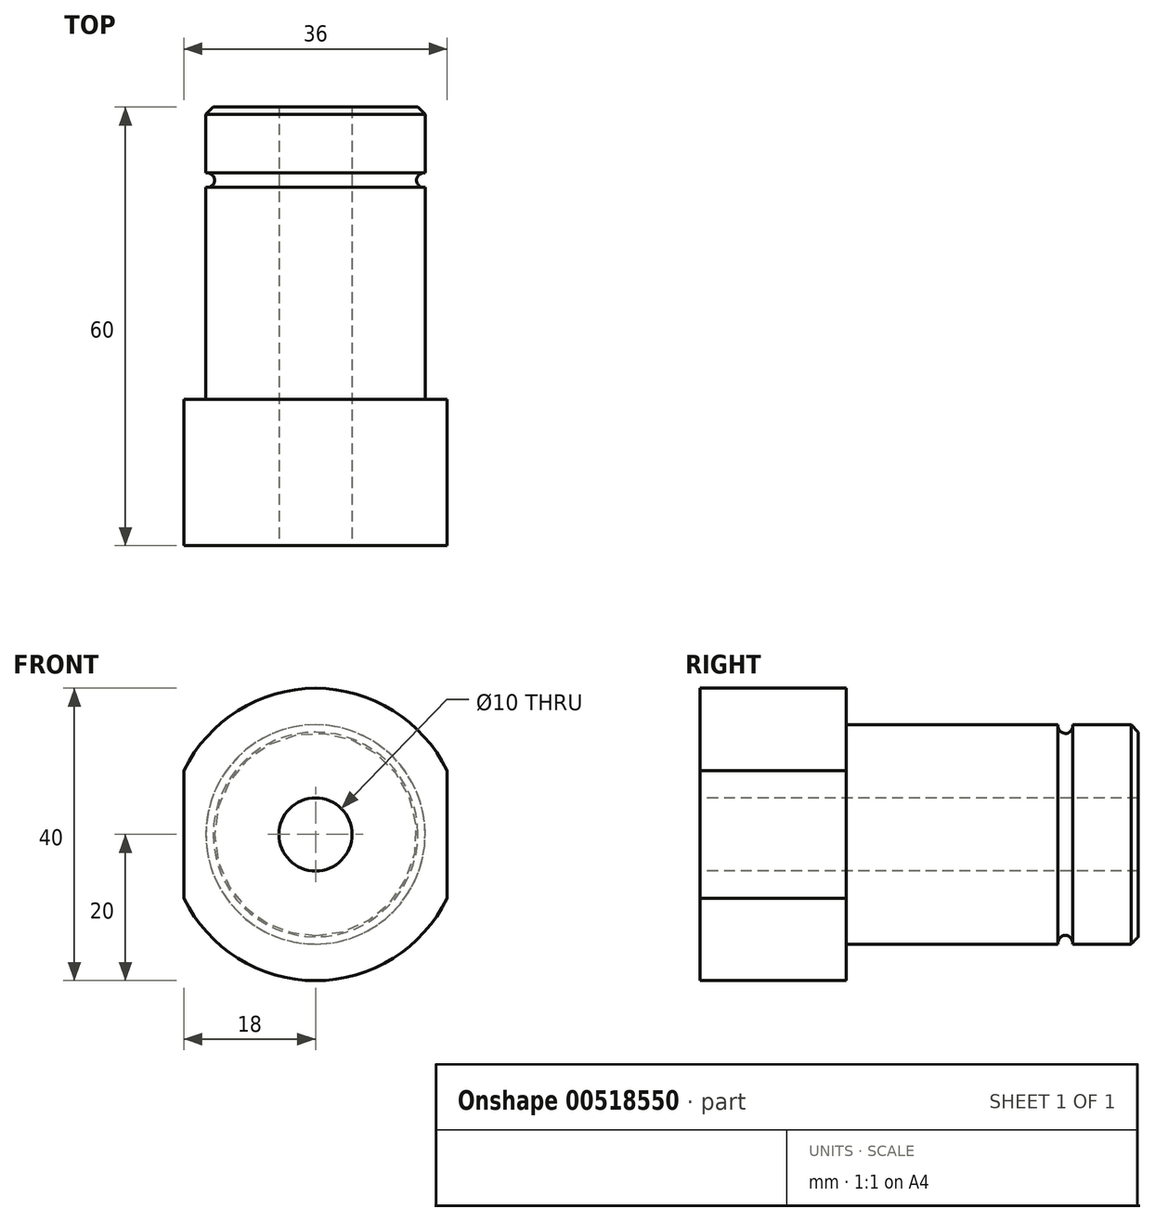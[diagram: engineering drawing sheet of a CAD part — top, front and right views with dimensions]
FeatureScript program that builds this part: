
annotation { "Feature Type Name" : "Feature", "Feature Type Description" : "" }
export const myFeature = defineFeature(function(context is Context, id is Id, definition is map)
    precondition{}
    {
        {
            var Q0;
            Q0=qCreatedBy(makeId("Front.planeOp"),FACE);
            var sketch = newSketch(context, id + "F0", { "sketchPlane" : qUnion([Q0])});
            skCircle(sketch, "E0", {"center": v(0, 0) * mm, "radius": 20 * mm});
            skSolve(sketch);
        }
        {
            var Q0;
            Q0=qCreatedBy(makeId("Right.planeOp"),FACE);
            var sketch = newSketch(context, id + "F1", { "sketchPlane" : qUnion([Q0])});
            skLineSegment(sketch, "E1", {"start": v(-36.37, 0) * mm, "end": v(46.3, 0) * mm});
            skSolve(sketch);
        }
        {
            var Q0;
            Q0 = qSketchRegion(id + "F0", true);
            extrude(context, id + "F2", {"entities" : qUnion([Q0]), "depth" : 20 * mm, "offsetDistance" : 25 * mm});
        }
        {
            var Q0;
            Q0=makeQuery(id+"F2.opExtrude","CAP_FACE",FACE,{"disambiguationData":[OSD([sQuery(id+"F0.wireOp",EDGE,"E0")])],"isStart":false});
            var sketch = newSketch(context, id + "F3", { "sketchPlane" : qUnion([Q0])});
            skLineSegment(sketch, "E2", {"start": v(-18, 8.72) * mm, "end": v(-18, -8.72) * mm});
            skSolve(sketch);
        }
        {
            var Q0;
            {var subQ0=sQuery(id+"F3.wireOp",EDGE,"E2");Q0=makeQuery(id+"F3.imprint","IMPRINT",FACE,{"disambiguationData":[TD([[makeQuery(id+"F3.imprint","IMPRINT",EDGE,{"derivedFrom":subQ0}),-1.0]])]});}
            extrude(context, id + "F4", {"entities" : qUnion([Q0]), "operationType" : NewBodyOperationType.REMOVE, "endBound" : BoundingType.THROUGH_ALL, "oppositeDirection" : true, "depth" : 25 * mm, "offsetDistance" : 25 * mm});
        }
        {
            var Q0;
            Q0=makeQuery(id+"F2.opExtrude","CAP_FACE",FACE,{"disambiguationData":[OSD([sQuery(id+"F0.wireOp",EDGE,"E0")])],"isStart":false});
            var sketch = newSketch(context, id + "F5", { "sketchPlane" : qUnion([Q0])});
            skLineSegment(sketch, "E3", {"start": v(18, 8.72) * mm, "end": v(18, -8.72) * mm});
            skSolve(sketch);
        }
        {
            var Q0;
            {var subQ0=sQuery(id+"F5.wireOp",EDGE,"E3");Q0=makeQuery(id+"F5.imprint","IMPRINT",FACE,{"disambiguationData":[TD([[makeQuery(id+"F5.imprint","IMPRINT",EDGE,{"derivedFrom":subQ0}),1.0]])]});}
            extrude(context, id + "F6", {"entities" : qUnion([Q0]), "operationType" : NewBodyOperationType.REMOVE, "endBound" : BoundingType.THROUGH_ALL, "oppositeDirection" : true, "depth" : 25 * mm, "offsetDistance" : 25 * mm});
        }
        {
            var Q0;
            Q0=makeQuery(id+"F2.opExtrude","CAP_FACE",FACE,{"disambiguationData":[OSD([sQuery(id+"F0.wireOp",EDGE,"E0")])],"isStart":false});
            var sketch = newSketch(context, id + "F7", { "sketchPlane" : qUnion([Q0])});
            skCircle(sketch, "E4", {"center": v(0, 0) * mm, "radius": 5 * mm});
            skSolve(sketch);
        }
        {
            var Q0;
            Q0=qCreatedBy(makeId("Right.planeOp"),FACE);
            var sketch = newSketch(context, id + "F8", { "sketchPlane" : qUnion([Q0])});
            skLineSegment(sketch, "E5.bottom", {"start": v(0, 0) * mm, "end": v(40, 0) * mm});
            skLineSegment(sketch, "E5.top", {"start": v(0, 15) * mm, "end": v(40, 15) * mm});
            skLineSegment(sketch, "E5.left", {"start": v(0, 0) * mm, "end": v(0, 15) * mm});
            skLineSegment(sketch, "E5.right", {"start": v(40, 0) * mm, "end": v(40, 15) * mm});
            skSolve(sketch);
        }
        {
            var Q0;
            Q0=makeQuery(id+"F8.imprint","IMPRINT",FACE,{"disambiguationData":[TD([[makeQuery(id+"F8.imprint","IMPRINT",EDGE,{"derivedFrom":sQuery(id+"F8.wireOp",EDGE,"E5.bottom")}),1.0]])]});
            var sketch = newSketch(context, id + "F9", { "sketchPlane" : qUnion([Q0])});
            skLineSegment(sketch, "E6", {"start": v(30, 16.86) * mm, "end": v(30, 12.78) * mm});
            skSolve(sketch);
        }
        {
            var Q0;
            Q0=makeQuery(id+"F8.imprint","IMPRINT",FACE,{"disambiguationData":[TD([[makeQuery(id+"F8.imprint","IMPRINT",EDGE,{"derivedFrom":sQuery(id+"F8.wireOp",EDGE,"E5.bottom")}),1.0]])]});
            var sketch = newSketch(context, id + "F10", { "sketchPlane" : qUnion([Q0])});
            skCircle(sketch, "E7", {"center": v(30, 14.82) * mm, "radius": 1 * mm});
            skSolve(sketch);
        }
        {
            var Q0;
            Q0=makeQuery(id+"F8.imprint","IMPRINT",FACE,{"disambiguationData":[TD([[makeQuery(id+"F8.imprint","IMPRINT",EDGE,{"derivedFrom":sQuery(id+"F8.wireOp",EDGE,"E5.bottom")}),1.0]])]});
            var Q1;
            Q1=sQuery(id+"F8.wireOp",EDGE,"E5.bottom");
            revolve(context, id + "F11", {"operationType" : NewBodyOperationType.ADD, "entities" : qUnion([Q0]), "axis" : qUnion([Q1]), "revolveType" : RevolveType.FULL});
        }
        {
            var Q0;
            Q0=makeQuery(id+"F11.opRevolve","SWEPT_EDGE",EDGE,{"disambiguationData":[OSD([sQuery(id+"F8.wireOp",EDGE,"E5.top"),sQuery(id+"F8.wireOp",EDGE,"E5.right")])]});
            chamfer(context, id + "F12", {"entities" : qUnion([Q0]), "width" : 1 * mm, "tangentPropagation" : true});
        }
        {
            var Q0;
            Q0=makeQuery(id+"F7.imprint","IMPRINT",FACE,{"disambiguationData":[TD([[makeQuery(id+"F7.imprint","IMPRINT",EDGE,{"derivedFrom":sQuery(id+"F7.wireOp",EDGE,"E4")}),1.0]])]});
            extrude(context, id + "F13", {"entities" : qUnion([Q0]), "operationType" : NewBodyOperationType.REMOVE, "endBound" : BoundingType.THROUGH_ALL, "oppositeDirection" : true, "depth" : 25 * mm, "offsetDistance" : 25 * mm});
        }
        {
            var Q0;
            Q0 = qSketchRegion(id + "F10", true);
            var Q1;
            Q1=sQuery(id+"F10.wireOp",EDGE,"E7");
            var Q2;
            Q2=sQuery(id+"F1.wireOp",EDGE,"E1");
            revolve(context, id + "F14", {"operationType" : NewBodyOperationType.REMOVE, "entities" : qUnion([Q0]), "surfaceEntities" : qUnion([Q1]), "axis" : qUnion([Q2]), "revolveType" : RevolveType.FULL, "oppositeDirection" : true});
        }
    });
